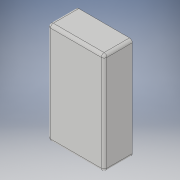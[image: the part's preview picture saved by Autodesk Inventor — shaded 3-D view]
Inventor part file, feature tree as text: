
AUTODESK INVENTOR PART (.ipt)
format: ipt  version: 2018 (Build 220112000, 112)  size: 321,536 bytes
history: native  units: in
note: dims shown in document units (in); Inventor stores cm internally (conversion verified against a paired STEP export)
features: sketch x10, extrude x9, fillet x4
ambient origin geometry x8: Origin, YZ Plane, XZ Plane, XY Plane, X Axis, Y Axis, Z Axis, Center Point
bodies: Solid1 (feature_tree)
feature tree (23):
  extrude  "Extrusion1"  Depth=4.0in
  extrude  "Extrusion2"  Depth=0.25in TaperAngle=0.0deg
  sketch  "Sketch3"  dims[d6=0.25in d7=0.0in d8=0.25in d9=0.0in]
  extrude  "Extrusion3"  Depth=0.25in TaperAngle=0.0deg
  extrude  "Extrusion4"  Depth=0.25in
  extrude  "Extrusion5"  Depth=0.25in
  extrude  "Extrusion6"  Depth=2.0in
  extrude  "Extrusion7"  Depth=0.25in
  extrude  "Extrusion8"  Depth=1.0in TaperAngle=0.0deg
  extrude  "Extrusion9"  Depth=0.25in
  fillet  "Fillet1"  Radius=2.25in
  fillet  "Fillet2"  Radius=1.0in
  fillet  "Fillet3"  Radius=0.25in
  fillet  "Fillet4"  Radius=2.25in
  sketch  "Sketch1"  dims[d0=2.0in d1=4.0in]
  sketch  "Sketch2"  dims[d2=0.25in d3=0.0in d4=0.25in d5=0.0in]
  sketch  "Sketch4"  dims[d10=0.25in d11=0.0in d12=0.25in]
  sketch  "Sketch5"  dims[d13=4.5in d14=0.25in]
  sketch  "Sketch6"  dims[d15=4.5in d16=2.0in]
  sketch  "Sketch7"  dims[d17=0.25in d18=0.25in]
  sketch  "Sketch8"  dims[d19=2.0in d20=1.0in d21=0.0in]
  sketch  "Sketch9"  dims[d22=1.0in d23=0.25in d24=2.25in d25=0.0in d26=1.0in d27=0.25in d28=2.25in d29=0.0in]
  sketch  "Sketch10"  dims[d30=0.25in d31=1.0in d32=4.0in d33=0.0in d34=0.125in d35=0.125in d36=0.125in d37=0.125in]
